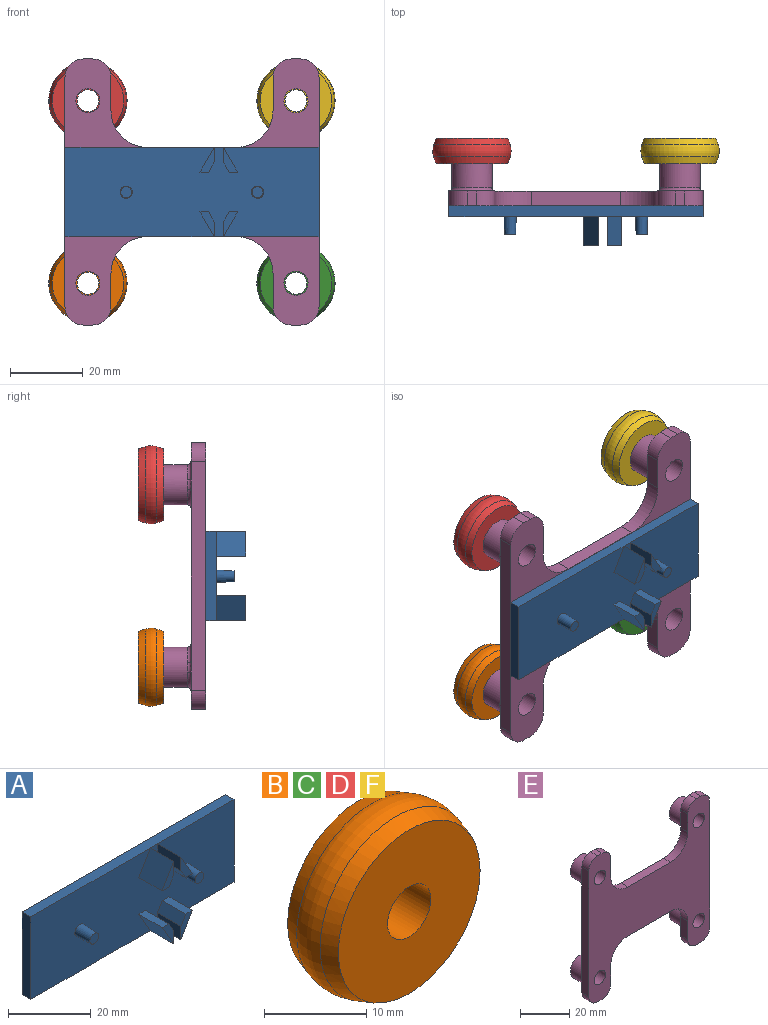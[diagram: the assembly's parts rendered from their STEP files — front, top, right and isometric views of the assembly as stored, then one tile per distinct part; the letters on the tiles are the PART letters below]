
ASSEMBLY  parts=6 mates=5
PART A: 34 faces, bbox 69.6x11x24.5 mm
  f0: cylinder r=10mm len=3mm, axis (0,-1,0), area 0.6mm2, adj f1,f7,f8,f9
  f1: plane 22.41x3mm, normal (0,0,-1), area 67.2mm2, adj f0,f2,f8,f9
  f2: plane 24.46x3mm, normal (1,0,0), area 73.4mm2, adj f1,f3,f8,f9
  f3: plane 69.6x3mm, normal (0,0,1), area 208.8mm2, adj f2,f4,f8,f9
  f4: plane 24.46x3mm, normal (-1,0,0), area 73.4mm2, adj f3,f5,f8,f9
  f5: plane 22.41x3mm, normal (0,0,-1), area 67.2mm2, adj f4,f6,f8,f9
  f6: cylinder r=10mm len=3mm, axis (0,-1,0), area 0.6mm2, adj f5,f7,f8,f9
  f7: plane 24.4x11mm, normal (0,0,-1), area 73.2mm2, adj f0,f6,f8,f9,f22,f23,f24,f25
  f8: plane 69.6x24.46mm, normal (0,-1,0), area 1640.3mm2, adj f0,f1,f2,f3,f4,f5,f6,f7
  f9: plane 69.6x24.46mm, normal (0,1,0), area 1702.1mm2, adj f0,f1,f2,f3,f4,f5,f6,f7
  f10: plane 8x2.78mm, normal (-0.87,0,-0.5), area 25.7mm2, adj f8,f11,f13,f14
  f11: plane 8x2.31mm, normal (0,0,-1), area 18.5mm2, adj f8,f10,f12,f14
  f12: plane 8x6.78mm, normal (0.87,0,0.5), area 62.6mm2, adj f8,f11,f13,f14
  f13: plane 8x4mm, normal (-1,0,0), area 32mm2, adj f8,f10,f12,f14
  f14: plane 6.78x3.92mm, normal (0,-1,0), area 11mm2, adj f10,f11,f12,f13
  f15: plane 8x6.78mm, normal (-0.87,0,0.5), area 62.6mm2, adj f8,f16,f18,f19
  f16: plane 8x2.31mm, normal (0,0,-1), area 18.5mm2, adj f8,f15,f17,f19
  f17: plane 8x2.78mm, normal (0.87,0,-0.5), area 25.7mm2, adj f8,f16,f18,f19
  f18: plane 8x4mm, normal (1,0,0), area 32mm2, adj f8,f15,f17,f19
  f19: plane 6.78x3.92mm, normal (0,-1,0), area 11mm2, adj f15,f16,f17,f18
  f20: plane 8x2.78mm, normal (0.87,0,0.5), area 25.7mm2, adj f8,f21,f23,f24
  f21: plane 8x2.31mm, normal (0,0,1), area 18.5mm2, adj f8,f20,f22,f24
  f22: plane 8x6.78mm, normal (-0.87,0,-0.5), area 62.6mm2, adj f7,f8,f21,f24
  f23: plane 8x4mm, normal (1,0,0), area 32mm2, adj f7,f8,f20,f24
  f24: plane 6.78x3.92mm, normal (0,-1,0), area 11mm2, adj f7,f20,f21,f22,f23
  f25: plane 8x6.78mm, normal (0.87,0,-0.5), area 62.6mm2, adj f7,f8,f26,f29
  f26: plane 8x2.31mm, normal (0,0,1), area 18.5mm2, adj f8,f25,f27,f29
  f27: plane 8x2.78mm, normal (-0.87,0,0.5), area 25.7mm2, adj f8,f26,f28,f29
  f28: plane 8x4mm, normal (-1,0,0), area 32mm2, adj f7,f8,f27,f29
  f29: plane 6.78x3.92mm, normal (0,-1,0), area 11mm2, adj f7,f25,f26,f27,f28
  f30: cone r=1.5mm half-angle=2deg, axis (0,1,0), area 49.9mm2, adj f8,f31
  f31: plane 3x3mm, normal (0,-1,0), area 7.1mm2, adj f30
  f32: cone r=1.5mm half-angle=2deg, axis (0,1,0), area 49.9mm2, adj f8,f33
  f33: plane 3x3mm, normal (0,-1,0), area 7.1mm2, adj f32
PART B: 6 faces, bbox 23.2x7x23.2 mm
  f0: cylinder r=3mm len=7mm, axis (0,-1,0), area 131.9mm2, adj f1,f4
  f1: plane 19.62x19.62mm, normal (0,1,0), area 274mm2, adj f0,f2
  f2: cone r=9.81mm half-angle=18.8deg, axis (0,-1,0), area 126.8mm2, adj f1,f5
  f3: cone r=11mm half-angle=18.8deg, axis (0,1,0), area 126.8mm2, adj f4,f5
  f4: plane 19.62x19.62mm, normal (0,-1,0), area 274mm2, adj f0,f3
  f5: torus R=5.72mm, axis (0,1,0), area 219.2mm2, adj f2,f3
PART C: same geometry as B
PART D: same geometry as B
PART E: 58 faces, bbox 72.1x11.5x72.9 mm
  f0: plane 12.6x9.85mm, normal (0,1,0), area 67.6mm2, adj f9,f10,f11,f38,f39,f44
  f1: plane 69.6x46.8mm, normal (0,1,0), area 2169.8mm2, adj f5,f6,f7,f9,f11,f12,f13,f15
  f2: plane 12.6x9.85mm, normal (0,1,0), area 67.6mm2, adj f7,f8,f9,f36,f37,f47
  f3: plane 12.6x9.85mm, normal (0,1,0), area 67.6mm2, adj f13,f14,f15,f40,f41,f56
  f4: plane 4x2.6mm, normal (0,0,-1), area 10.4mm2, adj f20,f21,f34,f35
  f5: plane 9.22x4.02mm, normal (1,0,0), area 36.8mm2, adj f1,f20,f21,f30,f35,f53
  f6: plane 24.4x4mm, normal (0,0,-1), area 97.6mm2, adj f1,f20,f30,f31
  f7: plane 9.22x4.02mm, normal (-1,0,0), area 36.8mm2, adj f1,f2,f20,f31,f36,f46
  f8: plane 4x2.6mm, normal (0,0,-1), area 10.4mm2, adj f2,f20,f36,f37
  f9: plane 62.92x4.02mm, normal (1,0,0), area 251.6mm2, adj f0,f1,f2,f20,f37,f38,f45,f49
  f10: plane 4x2.6mm, normal (0,0,1), area 10.4mm2, adj f0,f20,f38,f39
  f11: plane 9.22x4.02mm, normal (-1,0,0), area 36.8mm2, adj f0,f1,f20,f32,f39,f42
  f12: plane 24.4x4mm, normal (0,0,1), area 97.6mm2, adj f1,f20,f32,f33
  f13: plane 9.22x4.02mm, normal (1,0,0), area 36.8mm2, adj f1,f3,f20,f33,f40,f57
  f14: plane 4x2.6mm, normal (0,0,1), area 10.4mm2, adj f3,f20,f40,f41
  f15: plane 62.92x4.02mm, normal (-1,0,0), area 251.6mm2, adj f1,f3,f20,f21,f34,f41,f50,f54
  f16: cylinder r=3.3mm len=11.5mm, axis (0,-1,0), area 238.4mm2, adj f20,f23
  f17: cylinder r=3.3mm len=11.5mm, axis (0,-1,0), area 238.4mm2, adj f20,f29
  f18: cylinder r=3.3mm len=11.5mm, axis (0,-1,0), area 238.4mm2, adj f20,f27
  f19: cylinder r=3.3mm len=11.5mm, axis (0,-1,0), area 238.4mm2, adj f20,f25
  f20: plane 72.9x69.6mm, normal (0,-1,0), area 2831mm2, adj f4,f5,f6,f7,f8,f9,f10,f11
  f21: plane 12.6x9.85mm, normal (0,1,0), area 67.6mm2, adj f4,f5,f15,f34,f35,f51
  f22: cylinder r=5.5mm len=11mm, axis (0,-1,0), area 224.6mm2, adj f23,f54,f55,f56,f57
  f23: plane 11x11mm, normal (0,1,0), area 60.8mm2, adj f16,f22
  f24: cylinder r=5.5mm len=11mm, axis (0,-1,0), area 224.6mm2, adj f25,f50,f51,f52,f53
  f25: plane 11x11mm, normal (0,1,0), area 60.8mm2, adj f19,f24
  f26: cylinder r=5.5mm len=11mm, axis (0,-1,0), area 224.6mm2, adj f27,f46,f47,f48,f49
  f27: plane 11x11mm, normal (0,1,0), area 60.8mm2, adj f18,f26
  f28: cylinder r=5.5mm len=11mm, axis (0,-1,0), area 224.6mm2, adj f29,f42,f43,f44,f45
  f29: plane 11x11mm, normal (0,1,0), area 60.8mm2, adj f17,f28
  f30: cylinder r=10mm len=10mm, axis (0,1,0), area 62.8mm2, adj f1,f5,f6,f20
  f31: cylinder r=10mm len=10mm, axis (0,-1,0), area 62.8mm2, adj f1,f6,f7,f20
  f32: cylinder r=10mm len=10mm, axis (0,1,0), area 62.8mm2, adj f1,f11,f12,f20
  f33: cylinder r=10mm len=10mm, axis (0,-1,0), area 62.8mm2, adj f1,f12,f13,f20
  f34: cylinder r=5mm len=5mm, axis (0,-1,0), area 31.4mm2, adj f4,f15,f20,f21
  f35: cylinder r=5mm len=5mm, axis (0,-1,0), area 31.4mm2, adj f4,f5,f20,f21
  f36: cylinder r=5mm len=5mm, axis (0,-1,0), area 31.4mm2, adj f2,f7,f8,f20
  f37: cylinder r=5mm len=5mm, axis (0,1,0), area 31.4mm2, adj f2,f8,f9,f20
  f38: cylinder r=5mm len=5mm, axis (0,-1,0), area 31.4mm2, adj f0,f9,f10,f20
  f39: cylinder r=5mm len=5mm, axis (0,-1,0), area 31.4mm2, adj f0,f10,f11,f20
  f40: cylinder r=5mm len=5mm, axis (0,-1,0), area 31.4mm2, adj f3,f13,f14,f20
  f41: cylinder r=5mm len=5mm, axis (0,1,0), area 31.4mm2, adj f3,f14,f15,f20
  f42: bspline ~3.86x1.1mm, area 4.1mm2, adj f11,f28,f43,f44
  f43: torus R=6.5mm, axis (0,-1,0), area 24.4mm2, adj f1,f28,f42,f45
  f44: torus R=6.5mm, axis (0,-1,0), area 24.4mm2, adj f0,f28,f42,f45
  f45: bspline ~3.86x1.1mm, area 4.1mm2, adj f9,f28,f43,f44
  f46: bspline ~3.86x1.1mm, area 4.1mm2, adj f7,f26,f47,f48
  f47: torus R=6.5mm, axis (0,-1,0), area 24.4mm2, adj f2,f26,f46,f49
  f48: torus R=6.5mm, axis (0,-1,0), area 24.4mm2, adj f1,f26,f46,f49
  f49: bspline ~3.86x1.1mm, area 4.1mm2, adj f9,f26,f47,f48
  f50: bspline ~3.86x1.1mm, area 4.1mm2, adj f15,f24,f51,f52
  f51: torus R=6.5mm, axis (0,-1,0), area 24.4mm2, adj f21,f24,f50,f53
  f52: torus R=6.5mm, axis (0,-1,0), area 24.4mm2, adj f1,f24,f50,f53
  f53: bspline ~3.86x1.1mm, area 4.1mm2, adj f5,f24,f51,f52
  f54: bspline ~3.86x1.1mm, area 4.1mm2, adj f15,f22,f55,f56
  f55: torus R=6.5mm, axis (0,-1,0), area 24.4mm2, adj f1,f22,f54,f57
  f56: torus R=6.5mm, axis (0,-1,0), area 24.4mm2, adj f3,f22,f54,f57
  f57: bspline ~3.86x1.1mm, area 4.1mm2, adj f13,f22,f55,f56
PART F: same geometry as B
PLACE A t=(0,0,0.02)mm
PLACE B t=(-57,0,-50)mm
PLACE C t=(0,0,-50)mm
PLACE D t=(-57,0,0)mm
PLACE E at identity
PLACE F at identity
MATE fastened F.f0 <-> E.f17  axis (0,-1,0) through (80.8,227.82,318.28)mm
MATE fastened A.f9 <-> E.f20  axis (0,1,0) through (52.3,216.32,293.28)mm
MATE fastened D.f0 <-> E.f16  axis (0,-1,0) through (23.8,227.82,318.28)mm
MATE fastened C.f0 <-> E.f18  axis (0,-1,0) through (80.8,227.82,268.28)mm
MATE fastened B.f0 <-> E.f19  axis (0,-1,0) through (23.8,227.82,268.28)mm
